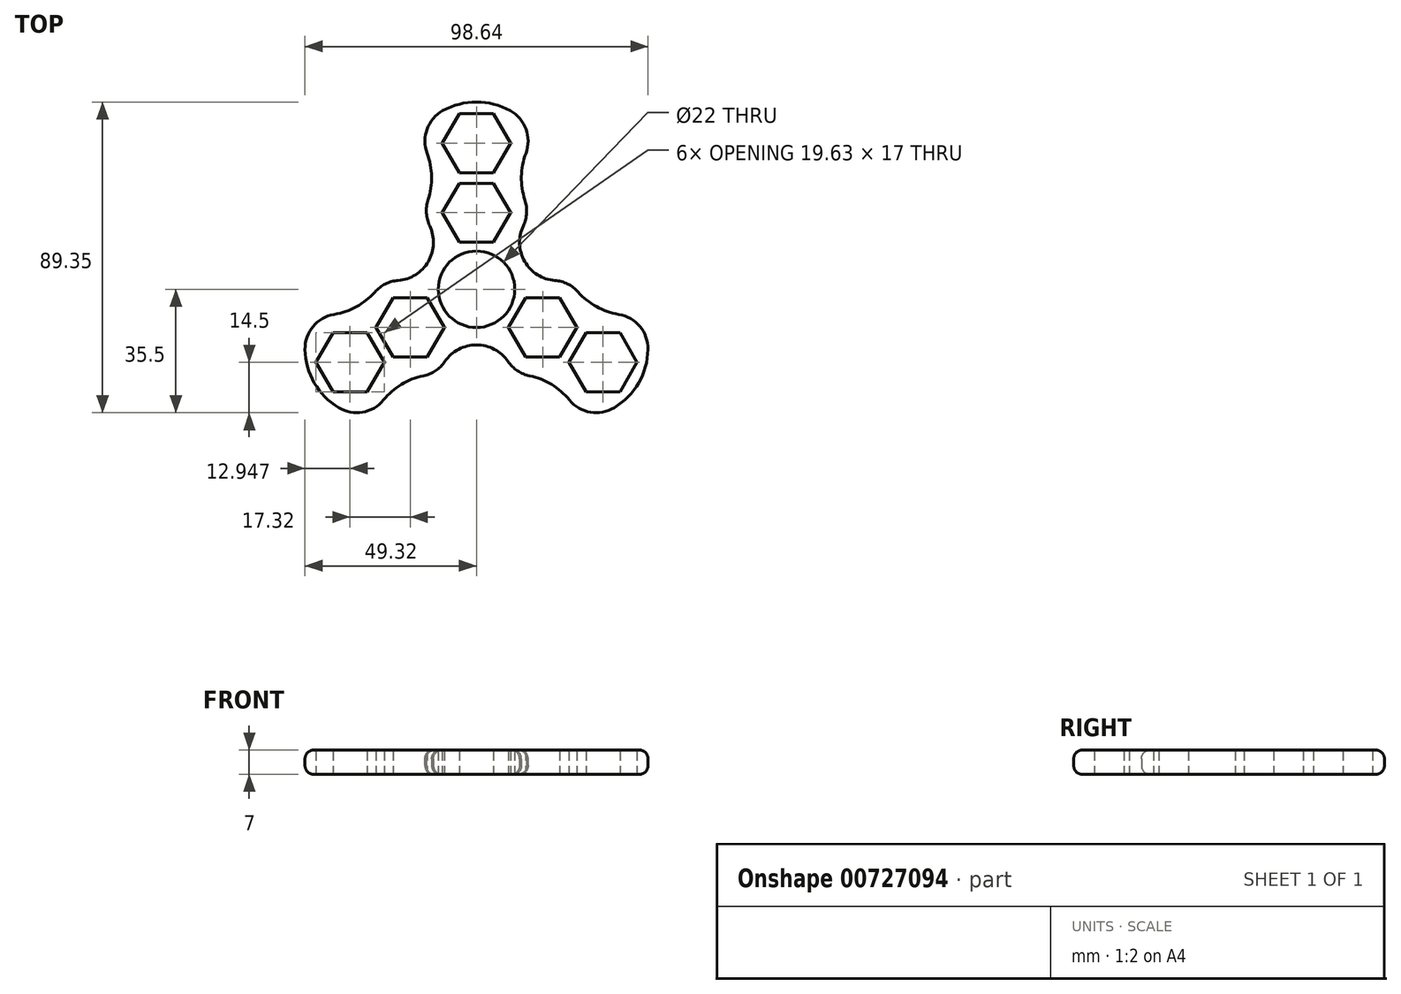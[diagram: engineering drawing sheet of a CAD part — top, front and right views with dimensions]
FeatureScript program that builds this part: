
annotation { "Feature Type Name" : "Feature", "Feature Type Description" : "" }
export const myFeature = defineFeature(function(context is Context, id is Id, definition is map)
    precondition{}
    {
        {
            var Q0;
            Q0=qCreatedBy(makeId("Top.planeOp"),FACE);
            var sketch = newSketch(context, id + "F0", { "sketchPlane" : qUnion([Q0])});
            skCircle(sketch, "E0", {"center": v(0, 0) * mm, "radius": 11 * mm});
            skLineSegment(sketch, "E1", {"start": v(0, 0) * mm, "end": v(-39.98, 23.08) * mm, "construction": true});
            skLineSegment(sketch, "E2.MirrorCS", {"start": v(0, 0) * mm, "end": v(39.98, 23.08) * mm, "construction": true});
            skLineSegment(sketch, "E3", {"start": v(0, 0) * mm, "end": v(0, -50.92) * mm, "construction": true});
            skArc(sketch, "E4", {"start": v(-25.49, 2.7) * mm, "mid": v(-13.86, 8) * mm, "end": v(-15.09, 20.72) * mm});
            skArc(sketch, "E5.MirrorC", {"start": v(25.49, 2.7) * mm, "mid": v(13.86, 8) * mm, "end": v(15.09, 20.72) * mm});
            skLineSegment(sketch, "E6.MirrorCS", {"start": v(0, 0) * mm, "end": v(39.98, -23.08) * mm, "construction": true});
            skArc(sketch, "E7.MirrorC", {"start": v(10.4, -23.43) * mm, "mid": v(0, -16) * mm, "end": v(-10.4, -23.43) * mm});
            skArc(sketch, "E8", {"start": v(-15.82, 21.61) * mm, "mid": v(-15.46, 21.16) * mm, "end": v(-15.09, 20.72) * mm});
            skArc(sketch, "E9.MirrorC", {"start": v(25.49, 2.7) * mm, "mid": v(26.06, 2.8) * mm, "end": v(26.63, 2.9) * mm});
            skCircle(sketch, "E10.cCircle", {"center": v(0, 22) * mm, "radius": 8.5 * mm, "construction": true});
            skLineSegment(sketch, "E10.0", {"start": v(-4.9, 30.5) * mm, "end": v(4.9, 30.5) * mm});
            skLineSegment(sketch, "E10.1", {"start": v(4.9, 30.5) * mm, "end": v(9.81, 22) * mm});
            skLineSegment(sketch, "E10.2", {"start": v(9.81, 22) * mm, "end": v(4.9, 13.5) * mm});
            skLineSegment(sketch, "E10.3", {"start": v(4.9, 13.5) * mm, "end": v(-4.9, 13.5) * mm});
            skLineSegment(sketch, "E10.4", {"start": v(-4.9, 13.5) * mm, "end": v(-9.81, 22) * mm});
            skLineSegment(sketch, "E10.5", {"start": v(-9.81, 22) * mm, "end": v(-4.9, 30.5) * mm});
            skPoint(sketch, "E10.0.midPoint", {"position": v(0, 30.5) * mm});
            skCircle(sketch, "E11.cCircle", {"center": v(0, 42) * mm, "radius": 8.5 * mm, "construction": true});
            skLineSegment(sketch, "E11.0", {"start": v(4.9, 33.5) * mm, "end": v(-4.9, 33.5) * mm});
            skLineSegment(sketch, "E11.1", {"start": v(-4.9, 33.5) * mm, "end": v(-9.81, 42) * mm});
            skLineSegment(sketch, "E11.2", {"start": v(-9.81, 42) * mm, "end": v(-4.9, 50.5) * mm});
            skLineSegment(sketch, "E11.3", {"start": v(-4.9, 50.5) * mm, "end": v(4.9, 50.5) * mm});
            skLineSegment(sketch, "E11.4", {"start": v(4.9, 50.5) * mm, "end": v(9.81, 42) * mm});
            skLineSegment(sketch, "E11.5", {"start": v(9.81, 42) * mm, "end": v(4.9, 33.5) * mm});
            skPoint(sketch, "E11.0.midPoint", {"position": v(0, 33.5) * mm});
            skLineSegment(sketch, "E12", {"start": v(0, 32) * mm, "end": v(-60.46, 32) * mm, "construction": true});
            skArc(sketch, "E13", {"start": v(-15.82, 21.61) * mm, "mid": v(-12.94, 33.12) * mm, "end": v(-17.1, 44.24) * mm});
            skArc(sketch, "E14.MirrorCS", {"start": v(15.82, 21.61) * mm, "mid": v(12.94, 33.12) * mm, "end": v(17.1, 44.24) * mm});
            skArc(sketch, "E15.MirrorCS", {"start": v(-26.63, 2.9) * mm, "mid": v(-35.16, -5.36) * mm, "end": v(-46.86, -7.32) * mm});
            skArc(sketch, "E16.MirrorCS", {"start": v(-10.8, -24.5) * mm, "mid": v(-22.22, -27.77) * mm, "end": v(-29.77, -36.92) * mm});
            skLineSegment(sketch, "E17.MirrorCS", {"start": v(-31.47, -29.5) * mm, "end": v(-26.56, -21) * mm});
            skLineSegment(sketch, "E18.MirrorCS", {"start": v(-26.56, -21) * mm, "end": v(-31.47, -12.5) * mm});
            skLineSegment(sketch, "E19.MirrorCS", {"start": v(-31.47, -12.5) * mm, "end": v(-41.28, -12.5) * mm});
            skLineSegment(sketch, "E20.MirrorCS", {"start": v(-41.28, -12.5) * mm, "end": v(-46.19, -21) * mm});
            skLineSegment(sketch, "E21.MirrorCS", {"start": v(-46.19, -21) * mm, "end": v(-41.28, -29.5) * mm});
            skLineSegment(sketch, "E22.MirrorCS", {"start": v(-41.28, -29.5) * mm, "end": v(-31.47, -29.5) * mm});
            skLineSegment(sketch, "E23.MirrorCS", {"start": v(-23.96, -19.5) * mm, "end": v(-14.15, -19.5) * mm});
            skLineSegment(sketch, "E24.MirrorCS", {"start": v(-28.87, -11) * mm, "end": v(-23.96, -19.5) * mm});
            skLineSegment(sketch, "E25.MirrorCS", {"start": v(-23.96, -2.5) * mm, "end": v(-28.87, -11) * mm});
            skLineSegment(sketch, "E26.MirrorCS", {"start": v(-14.15, -2.5) * mm, "end": v(-23.96, -2.5) * mm});
            skLineSegment(sketch, "E27.MirrorCS", {"start": v(-9.24, -11) * mm, "end": v(-14.15, -2.5) * mm});
            skArc(sketch, "E28.MirrorCS", {"start": v(-26.63, 2.9) * mm, "mid": v(-26.06, 2.8) * mm, "end": v(-25.49, 2.7) * mm});
            skLineSegment(sketch, "E29.MirrorCS", {"start": v(-14.15, -19.5) * mm, "end": v(-9.24, -11) * mm});
            skArc(sketch, "E30.trimOffspring", {"start": v(-10.4, -23.43) * mm, "mid": v(-10.6, -23.97) * mm, "end": v(-10.8, -24.5) * mm});
            skArc(sketch, "E31.trimOffspring", {"start": v(15.09, 20.72) * mm, "mid": v(15.46, 21.16) * mm, "end": v(15.82, 21.61) * mm});
            skArc(sketch, "E32.trimOffspring", {"start": v(-29.77, -36.92) * mm, "mid": v(-46.64, -26.93) * mm, "end": v(-46.86, -7.32) * mm});
            skArc(sketch, "E33.trimOffspring", {"start": v(17.1, 44.24) * mm, "mid": v(0, 53.85) * mm, "end": v(-17.1, 44.24) * mm});
            skArc(sketch, "E34.MirrorCS", {"start": v(10.8, -24.5) * mm, "mid": v(22.22, -27.77) * mm, "end": v(29.77, -36.92) * mm});
            skArc(sketch, "E35.MirrorCS", {"start": v(26.63, 2.9) * mm, "mid": v(35.16, -5.36) * mm, "end": v(46.86, -7.32) * mm});
            skLineSegment(sketch, "E36.MirrorCS", {"start": v(23.96, -2.5) * mm, "end": v(14.15, -2.5) * mm});
            skLineSegment(sketch, "E37.MirrorCS", {"start": v(28.87, -11) * mm, "end": v(23.96, -2.5) * mm});
            skLineSegment(sketch, "E38.MirrorCS", {"start": v(23.96, -19.5) * mm, "end": v(28.87, -11) * mm});
            skLineSegment(sketch, "E39.MirrorCS", {"start": v(14.15, -19.5) * mm, "end": v(23.96, -19.5) * mm});
            skLineSegment(sketch, "E40.MirrorCS", {"start": v(9.24, -11) * mm, "end": v(14.15, -19.5) * mm});
            skLineSegment(sketch, "E41.MirrorCS", {"start": v(26.56, -21) * mm, "end": v(31.47, -29.5) * mm});
            skLineSegment(sketch, "E42.MirrorCS", {"start": v(31.47, -29.5) * mm, "end": v(41.28, -29.5) * mm});
            skLineSegment(sketch, "E43.MirrorCS", {"start": v(41.28, -29.5) * mm, "end": v(46.19, -21) * mm});
            skLineSegment(sketch, "E44.MirrorCS", {"start": v(46.19, -21) * mm, "end": v(41.28, -12.5) * mm});
            skLineSegment(sketch, "E45.MirrorCS", {"start": v(41.28, -12.5) * mm, "end": v(31.47, -12.5) * mm});
            skLineSegment(sketch, "E46.MirrorCS", {"start": v(31.47, -12.5) * mm, "end": v(26.56, -21) * mm});
            skLineSegment(sketch, "E47.MirrorCS", {"start": v(14.15, -2.5) * mm, "end": v(9.24, -11) * mm});
            skArc(sketch, "E48.trimOffspring", {"start": v(46.86, -7.32) * mm, "mid": v(46.64, -26.93) * mm, "end": v(29.77, -36.92) * mm});
            skArc(sketch, "E49.trimOffspring", {"start": v(10.8, -24.5) * mm, "mid": v(10.6, -23.97) * mm, "end": v(10.4, -23.43) * mm});
            skSolve(sketch);
        }
        {
            var Q0;
            {var subQ0=sQuery(id+"F0.wireOp",EDGE,"443f7065-4032-4e26-a071-b725669880350.MirrorC");var subQ1=sQuery(id+"F0.wireOp",EDGE,"E0");var subQ2=makeQuery(id+"F0.imprint","INTERSECT",VERTEX,{"derivedFrom":[subQ1,subQ0]});Q0=makeQuery(id+"F0.imprint","IMPRINT",FACE,{"disambiguationData":[TD([[makeQuery(id+"F0.imprint","IMPRINT",EDGE,{"disambiguationData":[TD([[subQ2,1.0]])],"derivedFrom":subQ1}),-1.0]])]});}
            var Q1;
            Q1=makeQuery(id+"F0.imprint","IMPRINT",FACE,{"disambiguationData":[TD([[makeQuery(id+"F0.imprint","IMPRINT",EDGE,{"derivedFrom":sQuery(id+"F0.wireOp",EDGE,"3c77e0ad-56fd-488c-aca5-72fdf763e75a.0")}),1.0]])]});
            var Q2;
            {var subQ0=sQuery(id+"F0.wireOp",EDGE,"E8");var subQ1=sQuery(id+"F0.wireOp",EDGE,"E0");var subQ2=makeQuery(id+"F0.imprint","INTERSECT",VERTEX,{"derivedFrom":[subQ1,subQ0]});Q2=makeQuery(id+"F0.imprint","IMPRINT",FACE,{"disambiguationData":[TD([[makeQuery(id+"F0.imprint","IMPRINT",EDGE,{"disambiguationData":[TD([[subQ2,1.0]])],"derivedFrom":subQ1}),-1.0]])]});}
            var Q3;
            Q3=makeQuery(id+"F0.imprint","IMPRINT",FACE,{"disambiguationData":[TD([[makeQuery(id+"F0.imprint","IMPRINT",EDGE,{"derivedFrom":sQuery(id+"F0.wireOp",EDGE,"099a8888-4621-4fb9-b60a-3253a91fafc40.MirrorCS")}),-1.0]])]});
            var Q4;
            {var subQ0=sQuery(id+"F0.wireOp",EDGE,"443f7065-4032-4e26-a071-b725669880350.MirrorC");var subQ1=sQuery(id+"F0.wireOp",EDGE,"E0");var subQ2=makeQuery(id+"F0.imprint","INTERSECT",VERTEX,{"derivedFrom":[subQ1,subQ0]});Q4=makeQuery(id+"F0.imprint","IMPRINT",FACE,{"disambiguationData":[TD([[makeQuery(id+"F0.imprint","IMPRINT",EDGE,{"disambiguationData":[TD([[subQ2,-1.0]])],"derivedFrom":subQ1}),-1.0]])]});}
            var Q5;
            Q5=makeQuery(id+"F0.imprint","IMPRINT",FACE,{"disambiguationData":[TD([[makeQuery(id+"F0.imprint","IMPRINT",EDGE,{"derivedFrom":sQuery(id+"F0.wireOp",EDGE,"1659820b-f4e5-49e9-92a2-2dac94e12db50.MirrorCS")}),-1.0]])]});
            extrude(context, id + "F1", {"entities" : qUnion([Q0, Q1, Q2, Q3, Q4, Q5]), "depth" : 7 * mm, "offsetDistance" : 25 * mm});
        }
        {
            var Q0;
            Q0=makeQuery(id+"F1.opExtrude","SWEPT_EDGE",EDGE,{"disambiguationData":[OSD([sQuery(id+"F0.wireOp",EDGE,"E9.MirrorC"),sQuery(id+"F0.wireOp",EDGE,"E35.MirrorCS")])]});
            var Q1;
            Q1=makeQuery(id+"F1.opExtrude","SWEPT_EDGE",EDGE,{"disambiguationData":[OSD([sQuery(id+"F0.wireOp",EDGE,"E14.MirrorCS"),sQuery(id+"F0.wireOp",EDGE,"E31.trimOffspring")])]});
            var Q2;
            Q2=makeQuery(id+"F1.opExtrude","SWEPT_EDGE",EDGE,{"disambiguationData":[OSD([sQuery(id+"F0.wireOp",EDGE,"E35.MirrorCS"),sQuery(id+"F0.wireOp",EDGE,"E48.trimOffspring")])]});
            var Q3;
            Q3=makeQuery(id+"F1.opExtrude","SWEPT_EDGE",EDGE,{"disambiguationData":[OSD([sQuery(id+"F0.wireOp",EDGE,"E14.MirrorCS"),sQuery(id+"F0.wireOp",EDGE,"E33.trimOffspring")])]});
            var Q4;
            Q4=makeQuery(id+"F1.opExtrude","SWEPT_EDGE",EDGE,{"disambiguationData":[OSD([sQuery(id+"F0.wireOp",EDGE,"E13"),sQuery(id+"F0.wireOp",EDGE,"E33.trimOffspring")])]});
            var Q5;
            Q5=makeQuery(id+"F1.opExtrude","SWEPT_EDGE",EDGE,{"disambiguationData":[OSD([sQuery(id+"F0.wireOp",EDGE,"E8"),sQuery(id+"F0.wireOp",EDGE,"E13")])]});
            var Q6;
            Q6=makeQuery(id+"F1.opExtrude","SWEPT_EDGE",EDGE,{"disambiguationData":[OSD([sQuery(id+"F0.wireOp",EDGE,"E15.MirrorCS"),sQuery(id+"F0.wireOp",EDGE,"E28.MirrorCS")])]});
            var Q7;
            Q7=makeQuery(id+"F1.opExtrude","SWEPT_EDGE",EDGE,{"disambiguationData":[OSD([sQuery(id+"F0.wireOp",EDGE,"E15.MirrorCS"),sQuery(id+"F0.wireOp",EDGE,"E32.trimOffspring")])]});
            var Q8;
            Q8=makeQuery(id+"F1.opExtrude","SWEPT_EDGE",EDGE,{"disambiguationData":[OSD([sQuery(id+"F0.wireOp",EDGE,"E16.MirrorCS"),sQuery(id+"F0.wireOp",EDGE,"E32.trimOffspring")])]});
            var Q9;
            Q9=makeQuery(id+"F1.opExtrude","SWEPT_EDGE",EDGE,{"disambiguationData":[OSD([sQuery(id+"F0.wireOp",EDGE,"E16.MirrorCS"),sQuery(id+"F0.wireOp",EDGE,"E30.trimOffspring")])]});
            var Q10;
            Q10=makeQuery(id+"F1.opExtrude","SWEPT_EDGE",EDGE,{"disambiguationData":[OSD([sQuery(id+"F0.wireOp",EDGE,"E34.MirrorCS"),sQuery(id+"F0.wireOp",EDGE,"E49.trimOffspring")])]});
            var Q11;
            Q11=makeQuery(id+"F1.opExtrude","SWEPT_EDGE",EDGE,{"disambiguationData":[OSD([sQuery(id+"F0.wireOp",EDGE,"E34.MirrorCS"),sQuery(id+"F0.wireOp",EDGE,"E48.trimOffspring")])]});
            fillet(context, id + "F2", {"entities" : qUnion([Q0, Q1, Q2, Q3, Q4, Q5, Q6, Q7, Q8, Q9, Q10, Q11]), "radius" : 10 * mm, "tangentPropagation" : true, "allowEdgeOverflow" : false});
        }
        {
            var Q0;
            Q0=makeQuery(id+"F1.opExtrude","CAP_EDGE",EDGE,{"disambiguationData":[OSD([sQuery(id+"F0.wireOp",EDGE,"E8")])],"isStart":false});
            var Q1;
            Q1=makeQuery(id+"F1.opExtrude","CAP_EDGE",EDGE,{"disambiguationData":[OSD([sQuery(id+"F0.wireOp",EDGE,"E8")])],"isStart":true});
            var Q2;
            Q2=makeQuery(id+"F1.opExtrude","CAP_EDGE",EDGE,{"disambiguationData":[OSD([sQuery(id+"F0.wireOp",EDGE,"E5.MirrorC")])],"isStart":false});
            var Q3;
            Q3=makeQuery(id+"F1.opExtrude","CAP_EDGE",EDGE,{"disambiguationData":[OSD([sQuery(id+"F0.wireOp",EDGE,"E5.MirrorC")])],"isStart":true});
            var Q4;
            Q4=makeQuery(id+"F1.opExtrude","CAP_EDGE",EDGE,{"disambiguationData":[OSD([sQuery(id+"F0.wireOp",EDGE,"E9.MirrorC")])],"isStart":true});
            var Q5;
            Q5=makeQuery(id+"F1.opExtrude","CAP_EDGE",EDGE,{"disambiguationData":[OSD([sQuery(id+"F0.wireOp",EDGE,"E9.MirrorC")])],"isStart":false});
            var Q6;
            Q6=makeQuery(id+"F1.opExtrude","CAP_EDGE",EDGE,{"disambiguationData":[OSD([sQuery(id+"F0.wireOp",EDGE,"E7.MirrorC")])],"isStart":false});
            var Q7;
            Q7=makeQuery(id+"F1.opExtrude","CAP_EDGE",EDGE,{"disambiguationData":[OSD([sQuery(id+"F0.wireOp",EDGE,"E7.MirrorC")])],"isStart":true});
            var Q8;
            Q8=makeQuery(id+"F1.opExtrude","CAP_EDGE",EDGE,{"disambiguationData":[OSD([sQuery(id+"F0.wireOp",EDGE,"443f7065-4032-4e26-a071-b725669880350.MirrorC")])],"isStart":true});
            var Q9;
            Q9=makeQuery(id+"F1.opExtrude","CAP_EDGE",EDGE,{"disambiguationData":[OSD([sQuery(id+"F0.wireOp",EDGE,"443f7065-4032-4e26-a071-b725669880350.MirrorC")])],"isStart":false});
            var Q10;
            Q10=makeQuery(id+"F1.opExtrude","CAP_EDGE",EDGE,{"disambiguationData":[OSD([sQuery(id+"F0.wireOp",EDGE,"E4")])],"isStart":false});
            var Q11;
            Q11=makeQuery(id+"F1.opExtrude","CAP_EDGE",EDGE,{"disambiguationData":[OSD([sQuery(id+"F0.wireOp",EDGE,"E4")])],"isStart":true});
            fillet(context, id + "F3", {"entities" : qUnion([Q0, Q1, Q2, Q3, Q4, Q5, Q6, Q7, Q8, Q9, Q10, Q11]), "radius" : 2.5 * mm, "tangentPropagation" : true, "allowEdgeOverflow" : false});
        }
    });
